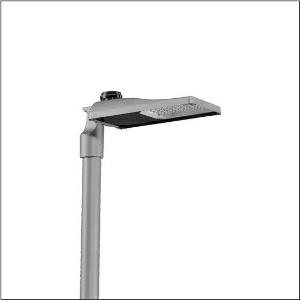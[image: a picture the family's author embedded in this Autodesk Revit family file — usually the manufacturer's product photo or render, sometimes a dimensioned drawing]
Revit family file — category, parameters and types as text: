
# Revit family: streetlight_sl_31_mini___st1_0a_5xh2d35n08ja_775f
name_source: partatom
category: Lighting Fixtures
units: mm (PartAtom-declared; Revit-internal decimal feet)

## family parameters
Cut with Voids When Loaded = No
Host = Face
Light Source = No
Part Type = Normal
Room Calculation Point = No
Round Connector Dimension = Use Diameter
Shared = No

## types (1)
- --- (1 x LED, 12140 lm, 81.1 W, 3000K)
    Apparent Load = 81 VA
    CIE Flux Codes = 40 73 97 100 100
    Color Rendering = 70
    Color Temperature = 3000K
    Default Elevation = 1800 mm
    Description = Streetlight SL 31 mini NEMA (7pin), Desk-Remote mast luminaire for post-top, side-entry; light control with lens of PMMA; light distribution: ST1.0a, direct asymmetric distribution, for standard-compliant lighting for roads and squares; LED: luminous flux: 12.140lm, light colour: 730, colour temperature: 3000K; luminous efficacy: 149,7lm/W; control: pre-setting: linear dimming characteristic, flexible luminous flux parameterisation, time-dependent luminous flux control, constant luminous flux control, intelligent temperature release in ECG and LED module, overheat protection; luminaire housing, of diecast aluminium, SITECO metallic grey (DB 702S), corrosivity category C5 high according to DIN EN ISO 12944; cover of toughened safety glass, transparent, mast flange of diecast aluminium, SITECO metallic grey (DB 702S), spigot size: 76/60mm, mast flange included unmounted; cable length: 10,5m, connection cable pre-assembled; mains connection: 220..240V, AC, 50/60Hz; power consumption (at start of service life): 81,1W / (at end of service life): 88,3W / (with reduced operation 50%): 36,4W; protection rating (complete): IP66; insulation class (complete): insulation class I (protective earthing); impact resistance: IK10; certification: CE, ENEC, ENEC+, VDE, UKCA; permissible operating ambient temperature for outdoor applications: -40..+50°C; packaging unit: 1 piece

Light Distribution: ST1.0a
    Height = 76 mm
    Lamp = 1 x LED
    Lamp Light Flux = 12140 lm
    Lamp Power = 81.1 W
    Lamp count = 1
    Length = 547 mm
    Luminous efficacy = 150 lm/W
    Manufacturer = Siteco
    ModVariant = No
    Model = 5XH2D35N08JA
    Number of Poles = 1
    OnlyDefault = Yes
    Power Factor = 1
    Product Name = Streetlight SL 31 mini | ST1.0a
    Product group = mast luminaire | pylon top
    ProductGroupID = 6100
    Protection Class = Protection class I
    Protection Degree = IP 66
    RLX_Detail_Level = 1
    RLX_Emergency_Light_Flux = 0 lm
    RLX_Emergency_Type = 0
    RLX_Emergency_Type_DB = No
    RlxData = <blob elided: 40369 chars, md5=add46a9b>
    Socket = socket
    Standby Power = 0 W
    System Light Flux = 12140 lm
    System Power = 81 W
    Type Comments = factory setting: luminous flux: 100 % | dim-lin: 254 | 860 mA
    Type Image = l_1300322.jpg
    URL = http://relux.com
    VarID = @adj_057555
    Voltage = 0 V
    Weight = 0.00 kg
    Width = 265 mm

## geometry (parser evidence)
native form markers: Blend x4, Sweep x8
no freeform markers — native parametric forms only
